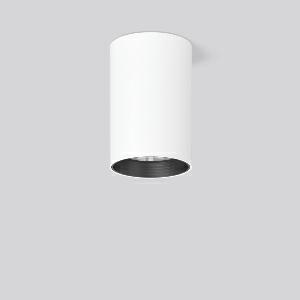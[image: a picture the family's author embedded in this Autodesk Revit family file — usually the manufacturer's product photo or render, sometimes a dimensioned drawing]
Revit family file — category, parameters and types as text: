
# Revit family: heledon_maxi_a_931250_002_2_76_0522
name_source: partatom
category: Lighting Fixtures
units: mm (PartAtom-declared; Revit-internal decimal feet)

## family parameters
Cut with Voids When Loaded = No
Host = Face
Light Source = No
Part Type = Normal
Room Calculation Point = No
Round Connector Dimension = Use Diameter
Shared = No

## types (1)
- HELEDON maxi A (1 x LED Modul 927 bakery, 2900 lm, 2700)
    Apparent Load = 33 VA
    Approval mark = CE
    CIE Flux Codes = 96 99 100 100 100
    Color Rendering = 90
    Color Temperature = 2700
    Default Elevation = 1800 mm
    Description = Series: HELEDON maxi
Cylindrical surface-mounted downlight. Housing: die-cast aluminium, powder-coated. Internal ceiling frame polycarbonate with bayonet mounting. Black plastic ring and recessed LED to prevent glare from the side. Optical assembly with lens made of plastic (polycarbonate) for the best homogeneous light distribution - can be changed without tools. Special LED for illumination of pastries included. Suitable for Ceiling mounting. Easy installation with a separate ceiling frame with bayonet mounting and plug connection. Driver integrated. Connected via plug-in connector. High quality converter without flickering and stroboscopic effect. The following accessories can be mounted without use of tools: interchangeable lenses, decorative glasses, honeycomb louvre, clear and frosted diffusers, white interchangeable plastic ring. 
Colour: traffic white, matt (RAL 9016)
Diameter: 123 mm
Height: 183 mm
Lamp: LED
Socket: without socket
Colour temperature: bakery
Colour rendering index (CRI): 97
System power: 33 W
Rated luminous flux: 2900 lm
Luminous efficiency: 88 lm/W
Control gear: Converter, dimmable, DALI
Protection class: I
Type of protection: IP 20
    Height = 183 mm
    Lamp = 1 x LED Modul 927 bakery
    Lamp Light Flux = 2900 lm
    Lamp count = 1
    Length = 123 mm
    Lifetime = 50000 h
    Luminous efficacy = 88 lm/W
    Manufacturer = RZB
    ModVariant = No
    Model = 931250.002.2.76
    Mounting Place = Ceiling
    Mounting Type = Surface mounted
    Number of Poles = 1
    OnlyDefault = Yes
    Power Factor = 1
    Product Name = HELEDON maxi A
    Product group = Surface mounted downlights
    ProductGroupID = 302
    Protection Class = Protection class I
    Protection Degree = IP 20
    RLX_Detail_Level = 1
    RLX_Emergency_Light_Flux = 0 lm
    RLX_Emergency_Type = 0
    RLX_Emergency_Type_DB = No
    RlxData = <blob elided: 97777 chars, md5=5f633092>
    Socket = socket
    Standby Power = 0 W
    System Light Flux = 2900 lm
    System Power = 33 W
    Type Comments = Product without accessories
    Type Image = 931193.002.jpg
    URL = http://relux.com
    VarID = ---
    Voltage = 230 V
    Voltage Range = 220-240 V
    Weight = 0.00 kg
    Width = 0 mm  [stored 0 ft]

note: [stored X ft] marks values corroborated as IEEE doubles in the binary element streams (Revit-internal decimal feet)

## geometry (parser evidence)
native form markers: Blend x4, Sweep x10
no freeform markers — native parametric forms only
